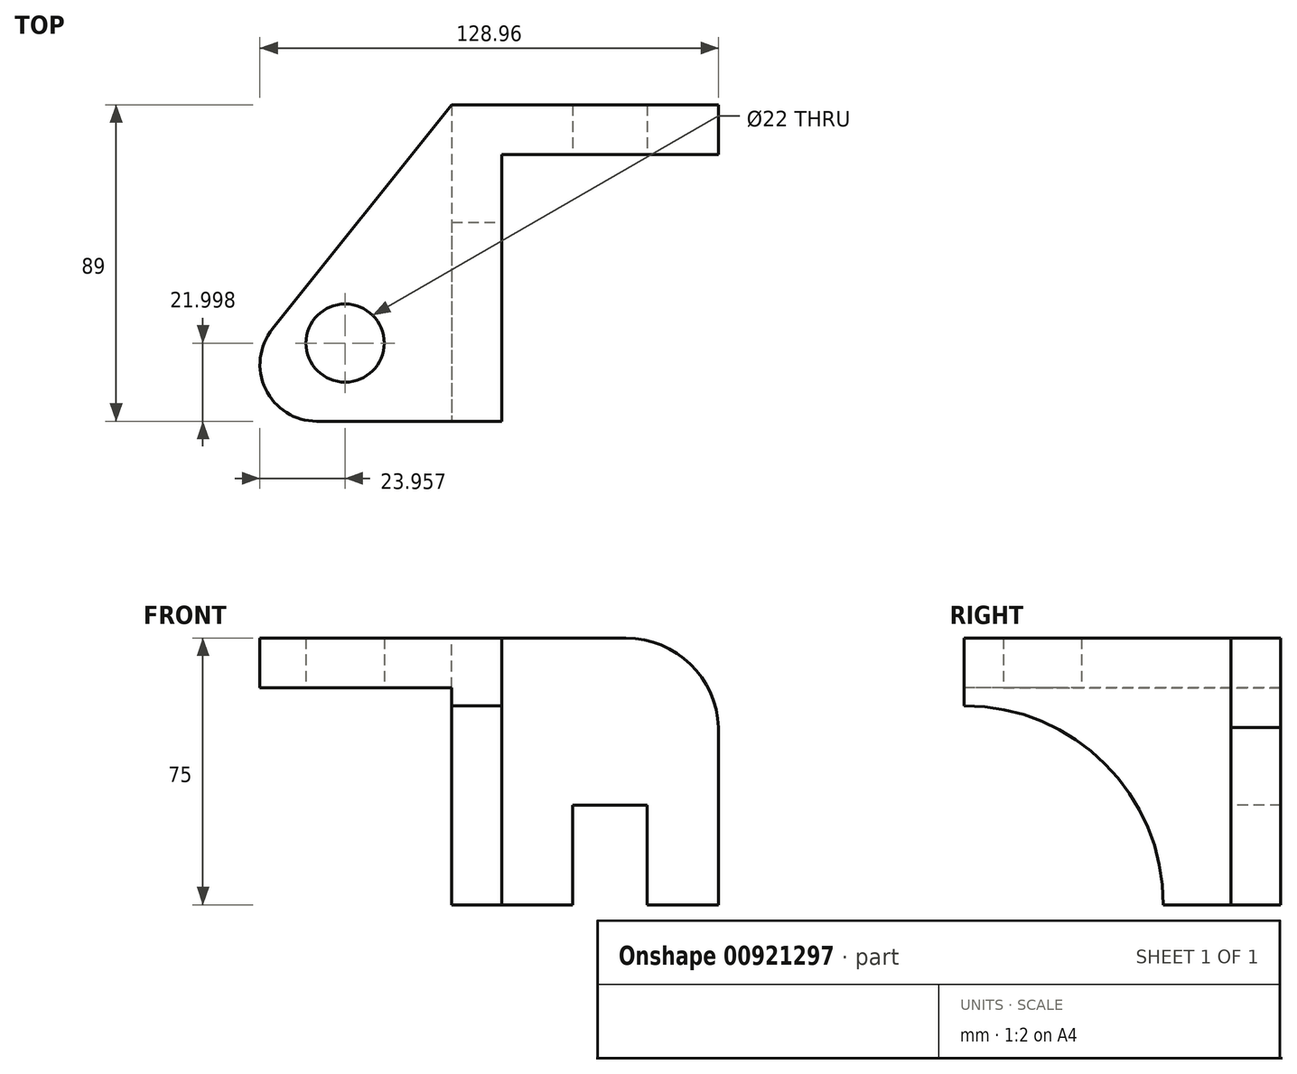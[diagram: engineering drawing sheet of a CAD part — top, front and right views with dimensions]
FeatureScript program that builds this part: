
annotation { "Feature Type Name" : "Feature", "Feature Type Description" : "" }
export const myFeature = defineFeature(function(context is Context, id is Id, definition is map)
    precondition{}
    {
        {
            var Q0;
            Q0=qCreatedBy(makeId("Top.planeOp"),FACE);
            var sketch = newSketch(context, id + "F0", { "sketchPlane" : qUnion([Q0])});
            skLineSegment(sketch, "E0", {"start": v(-24.41, 63.02) * mm, "end": v(50.59, 63.02) * mm});
            skLineSegment(sketch, "E1", {"start": v(-24.41, 63.02) * mm, "end": v(-24.41, -25.98) * mm});
            skLineSegment(sketch, "E2", {"start": v(-10.41, -25.98) * mm, "end": v(-10.41, 49.02) * mm});
            skLineSegment(sketch, "E3", {"start": v(-10.41, 49.02) * mm, "end": v(50.59, 49.02) * mm});
            skLineSegment(sketch, "E4", {"start": v(50.59, 49.02) * mm, "end": v(50.59, 63.02) * mm});
            skLineSegment(sketch, "E5", {"start": v(-24.41, -25.98) * mm, "end": v(-10.41, -25.98) * mm});
            skSolve(sketch);
        }
        {
            var Q0;
            Q0=makeQuery(id+"F0.imprint","IMPRINT",FACE,{"disambiguationData":[TD([[makeQuery(id+"F0.imprint","IMPRINT",EDGE,{"derivedFrom":sQuery(id+"F0.wireOp",EDGE,"E0")}),-1.0]])]});
            extrude(context, id + "F1", {"entities" : qUnion([Q0]), "oppositeDirection" : true, "depth" : 75 * mm, "offsetDistance" : 25.4 * mm});
        }
        {
            var Q0;
            Q0=makeQuery(id+"F1.opExtrude","SWEPT_FACE",FACE,{"disambiguationData":[OSD([sQuery(id+"F0.wireOp",EDGE,"E3")])]});
            var sketch = newSketch(context, id + "F2", { "sketchPlane" : qUnion([Q0])});
            skLineSegment(sketch, "E6.bottom", {"start": v(9.59, -75) * mm, "end": v(30.59, -75) * mm});
            skLineSegment(sketch, "E6.top", {"start": v(9.59, -47) * mm, "end": v(30.59, -47) * mm});
            skLineSegment(sketch, "E6.left", {"start": v(9.59, -75) * mm, "end": v(9.59, -47) * mm});
            skLineSegment(sketch, "E6.right", {"start": v(30.59, -75) * mm, "end": v(30.59, -47) * mm});
            skSolve(sketch);
        }
        {
            var Q0;
            Q0=makeQuery(id+"F2.imprint","IMPRINT",FACE,{"disambiguationData":[TD([[makeQuery(id+"F2.imprint","IMPRINT",EDGE,{"derivedFrom":sQuery(id+"F2.wireOp",EDGE,"E6.bottom")}),1.0]])]});
            extrude(context, id + "F3", {"entities" : qUnion([Q0]), "operationType" : NewBodyOperationType.REMOVE, "oppositeDirection" : true, "depth" : 14 * mm, "offsetDistance" : 25.4 * mm});
        }
        {
            var Q0;
            Q0=makeQuery(id+"F1.opExtrude","SWEPT_FACE",FACE,{"disambiguationData":[OSD([sQuery(id+"F0.wireOp",EDGE,"E2")])]});
            var sketch = newSketch(context, id + "F4", { "sketchPlane" : qUnion([Q0])});
            skArc(sketch, "E7", {"start": v(30.02, -75) * mm, "mid": v(13.62, -35.4) * mm, "end": v(-25.98, -19) * mm});
            skSolve(sketch);
        }
        {
            var Q0;
            {var subQ0=sQuery(id+"F4.wireOp",EDGE,"E7");Q0=makeQuery(id+"F4.imprint","IMPRINT",FACE,{"disambiguationData":[TD([[makeQuery(id+"F4.imprint","IMPRINT",EDGE,{"derivedFrom":subQ0}),1.0]])]});}
            extrude(context, id + "F5", {"entities" : qUnion([Q0]), "operationType" : NewBodyOperationType.REMOVE, "oppositeDirection" : true, "depth" : 14 * mm, "offsetDistance" : 25.4 * mm});
        }
        {
            var Q0;
            Q0=makeQuery(id+"F1.opExtrude","CAP_FACE",FACE,{"disambiguationData":[OSD([sQuery(id+"F0.wireOp",EDGE,"E0"),sQuery(id+"F0.wireOp",EDGE,"E1"),sQuery(id+"F0.wireOp",EDGE,"E2"),sQuery(id+"F0.wireOp",EDGE,"E3"),sQuery(id+"F0.wireOp",EDGE,"E4"),sQuery(id+"F0.wireOp",EDGE,"E5")])],"isStart":true});
            var sketch = newSketch(context, id + "F6", { "sketchPlane" : qUnion([Q0])});
            skLineSegment(sketch, "E8", {"start": v(-24.41, -25.98) * mm, "end": v(-62.41, -25.98) * mm});
            skArc(sketch, "E9", {"start": v(-74.82, 0) * mm, "mid": v(-76.8, -16.9) * mm, "end": v(-62.41, -25.98) * mm});
            skLineSegment(sketch, "E10", {"start": v(-74.82, 0) * mm, "end": v(-24.41, 63.02) * mm});
            skSolve(sketch);
        }
        {
            var Q0;
            Q0=makeQuery(id+"F6.imprint","IMPRINT",FACE,{"disambiguationData":[TD([[makeQuery(id+"F6.imprint","IMPRINT",EDGE,{"derivedFrom":sQuery(id+"F6.wireOp",EDGE,"E8")}),-1.0]])]});
            extrude(context, id + "F7", {"entities" : qUnion([Q0]), "operationType" : NewBodyOperationType.ADD, "oppositeDirection" : true, "depth" : 14 * mm, "offsetDistance" : 25.4 * mm});
        }
        {
            var Q0;
            Q0=makeQuery(id+"F7.opExtrude","CAP_FACE",FACE,{"disambiguationData":[OSD([sQuery(id+"F0.wireOp",EDGE,"E1"),sQuery(id+"F6.wireOp",EDGE,"E8"),sQuery(id+"F6.wireOp",EDGE,"E9"),sQuery(id+"F6.wireOp",EDGE,"E10")])],"isStart":false});
            var sketch = newSketch(context, id + "F8", { "sketchPlane" : qUnion([Q0])});
            skCircle(sketch, "E11", {"center": v(-54.41, 3.98) * mm, "radius": 11 * mm});
            skSolve(sketch);
        }
        {
            var Q0;
            Q0=makeQuery(id+"F8.imprint","IMPRINT",FACE,{"disambiguationData":[TD([[makeQuery(id+"F8.imprint","IMPRINT",EDGE,{"derivedFrom":sQuery(id+"F8.wireOp",EDGE,"E11")}),1.0]])]});
            extrude(context, id + "F9", {"entities" : qUnion([Q0]), "operationType" : NewBodyOperationType.REMOVE, "oppositeDirection" : true, "depth" : 14 * mm, "offsetDistance" : 25.4 * mm});
        }
        {
            var Q0;
            Q0=makeQuery(id+"F1.opExtrude","SWEPT_FACE",FACE,{"disambiguationData":[OSD([sQuery(id+"F0.wireOp",EDGE,"E3")])]});
            var sketch = newSketch(context, id + "F10", { "sketchPlane" : qUnion([Q0])});
            skArc(sketch, "E12", {"start": v(50.59, -26.87) * mm, "mid": v(43.29, -7.92) * mm, "end": v(24.59, 0) * mm});
            skSolve(sketch);
        }
        {
            var Q0;
            {var subQ0=sQuery(id+"F10.wireOp",EDGE,"E12");var subQ1=sQuery(id+"F0.wireOp",EDGE,"E3");var subQ4=makeQuery(id+"F1.opExtrude","SWEPT_EDGE",EDGE,{"disambiguationData":[OSD([subQ1,sQuery(id+"F0.wireOp",EDGE,"E4")])]});var subQ5=makeQuery(id+"F10.imprint","INTERSECT",VERTEX,{"disambiguationData":[OD(1.0)],"derivedFrom":[subQ4,subQ0]});Q0=makeQuery(id+"F10.imprint","IMPRINT",FACE,{"disambiguationData":[TD([[makeQuery(id+"F10.imprint","IMPRINT",EDGE,{"disambiguationData":[TD([[subQ5,-1.0]])],"derivedFrom":subQ0}),-1.0]])]});}
            extrude(context, id + "F11", {"entities" : qUnion([Q0]), "operationType" : NewBodyOperationType.REMOVE, "oppositeDirection" : true, "depth" : 14 * mm, "offsetDistance" : 25.4 * mm});
        }
    });
